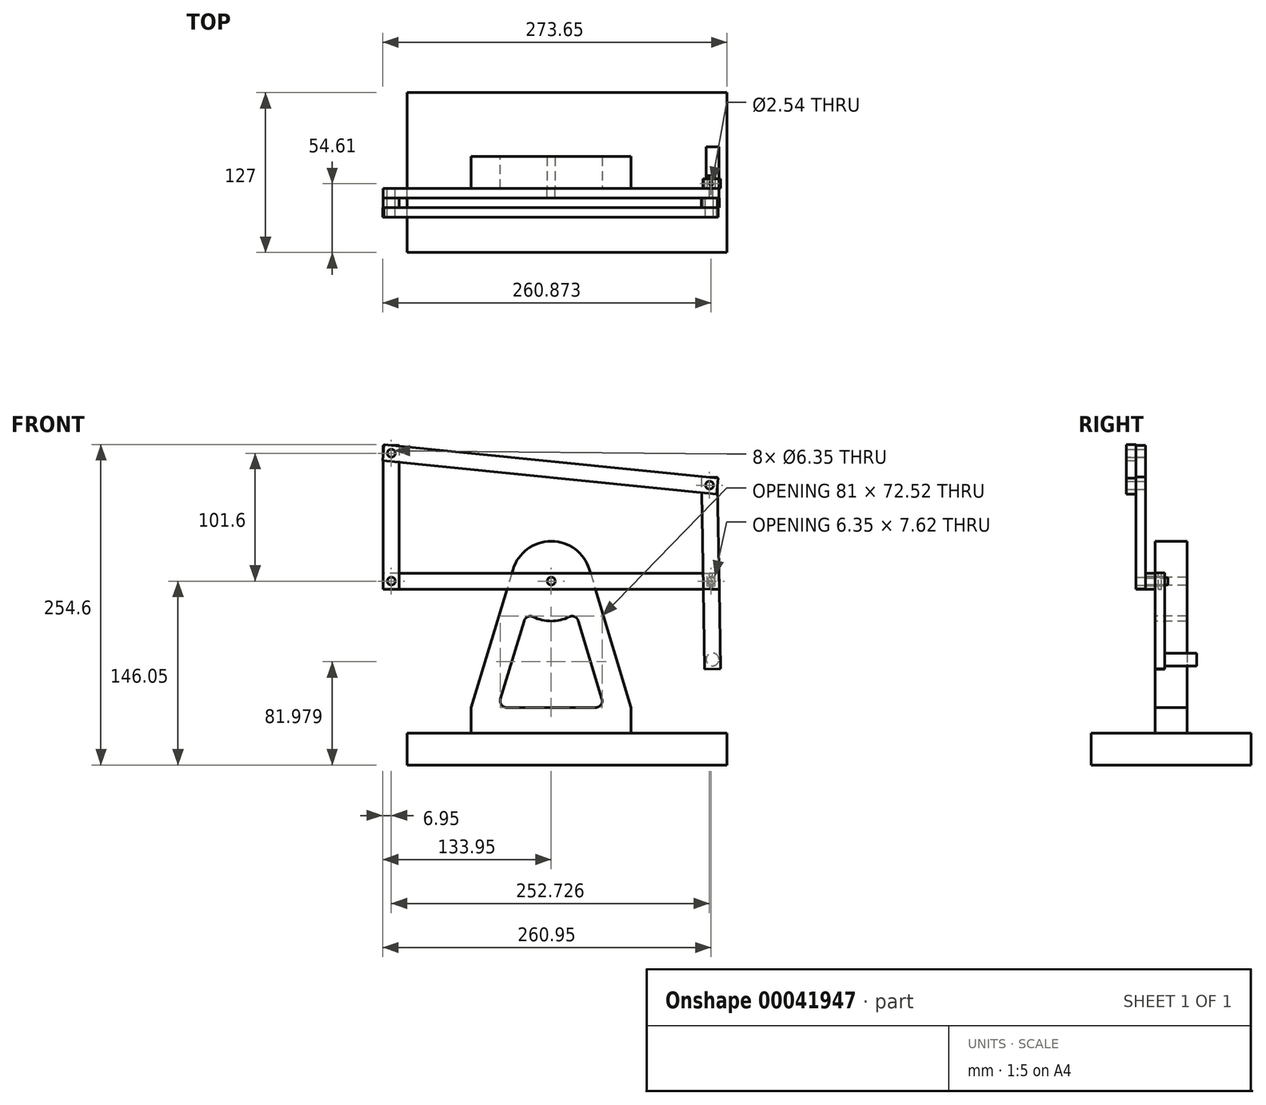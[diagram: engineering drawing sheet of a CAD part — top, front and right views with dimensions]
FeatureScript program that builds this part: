
annotation { "Feature Type Name" : "Feature", "Feature Type Description" : "" }
export const myFeature = defineFeature(function(context is Context, id is Id, definition is map)
    precondition{}
    {
        {
            var Q0;
            Q0=qCreatedBy(makeId("Top.planeOp"),FACE);
            var sketch = newSketch(context, id + "F0", { "sketchPlane" : qUnion([Q0])});
            skLineSegment(sketch, "E0.bottom", {"start": v(0, 0) * mm, "end": v(254, 0) * mm});
            skLineSegment(sketch, "E0.top", {"start": v(0, 127) * mm, "end": v(254, 127) * mm});
            skLineSegment(sketch, "E0.left", {"start": v(0, 0) * mm, "end": v(0, 127) * mm});
            skLineSegment(sketch, "E0.right", {"start": v(254, 0) * mm, "end": v(254, 127) * mm});
            skSolve(sketch);
        }
        {
            var Q0;
            Q0 = qSketchRegion(id + "F0", true);
            extrude(context, id + "F1", {"entities" : qUnion([Q0]), "depth" : 25.4 * mm});
        }
        {
            var Q0;
            Q0=makeQuery(id+"F1.opExtrude","SWEPT_FACE",FACE,{"disambiguationData":[OSD([sQuery(id+"F0.wireOp",EDGE,"E0.bottom")])]});
            var Q1;
            Q1=makeQuery(id+"F1.opExtrude","SWEPT_FACE",FACE,{"disambiguationData":[OSD([sQuery(id+"F0.wireOp",EDGE,"E0.top")])]});
            cPlane(context, id + "F2", {"entities" : qUnion([Q0, Q1]), "cplaneType" : CPlaneType.MID_PLANE, "offset" : 152.4 * mm, "width" : 152.4 * mm, "height" : 152.4 * mm});
        }
        {
            var Q0;
            Q0=qCreatedBy(id+"F2.planeOp",FACE);
            var sketch = newSketch(context, id + "F3", { "sketchPlane" : qUnion([Q0])});
            skLineSegment(sketch, "E1.bottom", {"start": v(50.8, 25.4) * mm, "end": v(177.8, 25.4) * mm});
            skLineSegment(sketch, "E1.top", {"start": v(50.8, 177.8) * mm, "end": v(177.8, 177.8) * mm});
            skLineSegment(sketch, "E1.left", {"start": v(50.8, 25.4) * mm, "end": v(50.8, 177.8) * mm});
            skLineSegment(sketch, "E1.right", {"start": v(177.8, 25.4) * mm, "end": v(177.8, 177.8) * mm});
            skSolve(sketch);
        }
        {
            var Q0;
            Q0 = qSketchRegion(id + "F3", true);
            extrude(context, id + "F4", {"entities" : qUnion([Q0]), "endBound" : BoundingType.SYMMETRIC, "depth" : 25.4 * mm});
        }
        {
            var Q0;
            Q0=makeQuery(id+"F4.opExtrude","CAP_FACE",FACE,{"disambiguationData":[OSD([sQuery(id+"F3.wireOp",EDGE,"E1.bottom"),sQuery(id+"F3.wireOp",EDGE,"E1.top"),sQuery(id+"F3.wireOp",EDGE,"E1.left"),sQuery(id+"F3.wireOp",EDGE,"E1.right")])],"isStart":false});
            var sketch = newSketch(context, id + "F5", { "sketchPlane" : qUnion([Q0])});
            skLineSegment(sketch, "E2", {"start": v(114.3, 25.4) * mm, "end": v(114.3, 177.8) * mm, "construction": true});
            skCircle(sketch, "E3", {"center": v(114.3, 146.05) * mm, "radius": 31.75 * mm});
            skLineSegment(sketch, "E4", {"start": v(83.9, 155.24) * mm, "end": v(50.8, 45.72) * mm});
            skLineSegment(sketch, "E5", {"start": v(144.7, 155.24) * mm, "end": v(177.8, 45.72) * mm});
            skLineSegment(sketch, "E6", {"start": v(50.8, 45.72) * mm, "end": v(177.8, 45.72) * mm});
            skCircle(sketch, "E7", {"center": v(114.3, 146.05) * mm, "radius": 11.43 * mm});
            skLineSegment(sketch, "E8", {"start": v(103.36, 149.36) * mm, "end": v(72.03, 45.72) * mm});
            skLineSegment(sketch, "E9", {"start": v(125.24, 149.36) * mm, "end": v(156.57, 45.72) * mm});
            skSolve(sketch);
        }
        {
            var Q0;
            {var subQ1=sQuery(id+"F5.wireOp",EDGE,"E3");var subQ5=sQuery(id+"F5.wireOp",EDGE,"E8");var subQ6=makeQuery(id+"F5.imprint","INTERSECT",VERTEX,{"derivedFrom":[subQ1,subQ5]});Q0=makeQuery(id+"F5.imprint","IMPRINT",FACE,{"disambiguationData":[TD([[makeQuery(id+"F5.imprint","IMPRINT",EDGE,{"disambiguationData":[TD([[subQ6,-1.0]])],"derivedFrom":subQ1}),-1.0]])]});}
            var Q1;
            {var subQ5=sQuery(id+"F5.wireOp",EDGE,"E4");Q1=makeQuery(id+"F5.imprint","IMPRINT",FACE,{"disambiguationData":[TD([[makeQuery(id+"F5.imprint","IMPRINT",EDGE,{"derivedFrom":subQ5}),-1.0]])]});}
            var Q2;
            {var subQ1=sQuery(id+"F5.wireOp",EDGE,"E5");Q2=makeQuery(id+"F5.imprint","IMPRINT",FACE,{"disambiguationData":[TD([[makeQuery(id+"F5.imprint","IMPRINT",EDGE,{"derivedFrom":subQ1}),1.0]])]});}
            extrude(context, id + "F6", {"entities" : qUnion([Q0, Q1, Q2]), "operationType" : NewBodyOperationType.REMOVE, "endBound" : BoundingType.THROUGH_ALL, "oppositeDirection" : true, "depth" : 25.4 * mm});
        }
        {
            var Q0;
            Q0=makeQuery(id+"F6.boolean.opBoolean","COPY",EDGE,{"derivedFrom":makeQuery(id+"F6.opExtrude","SWEPT_EDGE",EDGE,{"disambiguationData":[OSD([sQuery(id+"F5.wireOp",EDGE,"E6"),sQuery(id+"F5.wireOp",EDGE,"E8")])]})});
            var Q1;
            Q1=makeQuery(id+"F6.boolean.opBoolean","COPY",EDGE,{"derivedFrom":makeQuery(id+"F6.opExtrude","SWEPT_EDGE",EDGE,{"disambiguationData":[OSD([sQuery(id+"F5.wireOp",EDGE,"E6"),sQuery(id+"F5.wireOp",EDGE,"E9")])]})});
            var Q2;
            Q2=makeQuery(id+"F6.boolean.opBoolean","COPY",EDGE,{"derivedFrom":makeQuery(id+"F6.opExtrude","SWEPT_EDGE",EDGE,{"disambiguationData":[OSD([sQuery(id+"F5.wireOp",EDGE,"E3"),sQuery(id+"F5.wireOp",EDGE,"E8")])]})});
            var Q3;
            Q3=makeQuery(id+"F6.boolean.opBoolean","COPY",EDGE,{"derivedFrom":makeQuery(id+"F6.opExtrude","SWEPT_EDGE",EDGE,{"disambiguationData":[OSD([sQuery(id+"F5.wireOp",EDGE,"E3"),sQuery(id+"F5.wireOp",EDGE,"E9")])]})});
            fillet(context, id + "F7", {"entities" : qUnion([Q0, Q1, Q2, Q3]), "radius" : 5.08 * mm, "tangentPropagation" : true, "allowEdgeOverflow" : false});
        }
        {
            var Q0;
            Q0=makeQuery(id+"F4.opExtrude","CAP_FACE",FACE,{"disambiguationData":[OSD([sQuery(id+"F3.wireOp",EDGE,"E1.bottom"),sQuery(id+"F3.wireOp",EDGE,"E1.top"),sQuery(id+"F3.wireOp",EDGE,"E1.left"),sQuery(id+"F3.wireOp",EDGE,"E1.right")])],"isStart":false});
            var sketch = newSketch(context, id + "F8", { "sketchPlane" : qUnion([Q0])});
            skLineSegment(sketch, "E10", {"start": v(-12.7, 146.05) * mm, "end": v(241.3, 146.05) * mm, "construction": true});
            skPoint(sketch, "E11", {"position": v(114.3, 146.05) * mm});
            skLineSegment(sketch, "E12", {"start": v(-12.7, 146.05) * mm, "end": v(-12.7, 247.65) * mm, "construction": true});
            skLineSegment(sketch, "E13", {"start": v(-12.7, 247.65) * mm, "end": v(240.03, 222.24) * mm, "construction": true});
            skLineSegment(sketch, "E14", {"start": v(240.03, 222.24) * mm, "end": v(241.3, 146.05) * mm, "construction": true});
            skSolve(sketch);
        }
        {
            var Q0;
            {var subQ6=sQuery(id+"F3.wireOp",EDGE,"E1.bottom");Q0=makeQuery(id+"F8.imprint","IMPRINT",FACE,{"disambiguationData":[TD([[makeQuery(id+"F8.imprint","IMPRINT",EDGE,{"derivedFrom":makeQuery(id+"F4.opExtrude","CAP_EDGE",EDGE,{"disambiguationData":[OSD([subQ6])],"isStart":false})}),1.0]])]});}
            var sketch = newSketch(context, id + "F9", { "sketchPlane" : qUnion([Q0])});
            skLineSegment(sketch, "E15.rect.bottom", {"start": v(247.65, 139.7) * mm, "end": v(-19.05, 139.7) * mm});
            skLineSegment(sketch, "E15.rect.top", {"start": v(247.65, 152.4) * mm, "end": v(-19.05, 152.4) * mm});
            skLineSegment(sketch, "E15.rect.left", {"start": v(247.65, 139.7) * mm, "end": v(247.65, 152.4) * mm});
            skLineSegment(sketch, "E15.rect.right", {"start": v(-19.05, 139.7) * mm, "end": v(-19.05, 152.4) * mm});
            skPoint(sketch, "E15.rect.middle", {"position": v(114.3, 146.05) * mm});
            skSolve(sketch);
        }
        {
            var Q0;
            Q0 = qSketchRegion(id + "F9", true);
            extrude(context, id + "F10", {"entities" : qUnion([Q0]), "depth" : 7.62 * mm});
        }
        {
            var Q0;
            Q0=makeQuery(id+"F10.opExtrude","CAP_FACE",FACE,{"disambiguationData":[OSD([sQuery(id+"F9.wireOp",EDGE,"E15.rect.bottom"),sQuery(id+"F9.wireOp",EDGE,"E15.rect.top"),sQuery(id+"F9.wireOp",EDGE,"E15.rect.left"),sQuery(id+"F9.wireOp",EDGE,"E15.rect.right")])],"isStart":false});
            var sketch = newSketch(context, id + "F11", { "sketchPlane" : qUnion([Q0])});
            skLineSegment(sketch, "E16.rect.bottom", {"start": v(-6.35, 254) * mm, "end": v(-19.05, 254) * mm});
            skLineSegment(sketch, "E16.rect.top", {"start": v(-6.35, 139.7) * mm, "end": v(-19.05, 139.7) * mm});
            skLineSegment(sketch, "E16.rect.left", {"start": v(-6.35, 254) * mm, "end": v(-6.35, 139.7) * mm});
            skLineSegment(sketch, "E16.rect.right", {"start": v(-19.05, 254) * mm, "end": v(-19.05, 139.7) * mm});
            skPoint(sketch, "E16.rect.middle", {"position": v(-12.7, 196.85) * mm});
            skLineSegment(sketch, "E17", {"start": v(-12.7, 254) * mm, "end": v(-12.7, 139.7) * mm, "construction": true});
            skSolve(sketch);
        }
        {
            var Q0;
            Q0 = qSketchRegion(id + "F11", true);
            extrude(context, id + "F12", {"entities" : qUnion([Q0]), "depth" : 7.62 * mm});
        }
        {
            var Q0;
            Q0=makeQuery(id+"F12.opExtrude","CAP_FACE",FACE,{"disambiguationData":[OSD([sQuery(id+"F11.wireOp",EDGE,"E16.rect.bottom"),sQuery(id+"F11.wireOp",EDGE,"E16.rect.top"),sQuery(id+"F11.wireOp",EDGE,"E16.rect.left"),sQuery(id+"F11.wireOp",EDGE,"E16.rect.right")])],"isStart":false});
            var sketch = newSketch(context, id + "F13", { "sketchPlane" : qUnion([Q0])});
            skLineSegment(sketch, "E18.rect.bottom", {"start": v(245.7, 215.29) * mm, "end": v(-19.65, 241.97) * mm});
            skLineSegment(sketch, "E18.rect.top", {"start": v(246.98, 227.92) * mm, "end": v(-18.38, 254.6) * mm});
            skLineSegment(sketch, "E18.rect.left", {"start": v(245.7, 215.29) * mm, "end": v(246.98, 227.92) * mm});
            skLineSegment(sketch, "E18.rect.right", {"start": v(-19.65, 241.97) * mm, "end": v(-18.38, 254.6) * mm});
            skPoint(sketch, "E18.rect.middle", {"position": v(113.66, 234.94) * mm});
            skLineSegment(sketch, "E19", {"start": v(246.34, 221.6) * mm, "end": v(-19.02, 248.29) * mm, "construction": true});
            skSolve(sketch);
        }
        {
            var Q0;
            Q0 = qSketchRegion(id + "F13", true);
            extrude(context, id + "F14", {"entities" : qUnion([Q0]), "depth" : 7.62 * mm});
        }
        {
            var Q0;
            Q0=makeQuery(id+"F10.opExtrude","CAP_FACE",FACE,{"disambiguationData":[OSD([sQuery(id+"F9.wireOp",EDGE,"E15.rect.bottom"),sQuery(id+"F9.wireOp",EDGE,"E15.rect.top"),sQuery(id+"F9.wireOp",EDGE,"E15.rect.left"),sQuery(id+"F9.wireOp",EDGE,"E15.rect.right")])],"isStart":false});
            var sketch = newSketch(context, id + "F15", { "sketchPlane" : qUnion([Q0])});
            skLineSegment(sketch, "E20.rect.bottom", {"start": v(246.27, 228.7) * mm, "end": v(233.57, 228.48) * mm});
            skLineSegment(sketch, "E20.rect.top", {"start": v(247.76, 139.8) * mm, "end": v(235.06, 139.6) * mm});
            skLineSegment(sketch, "E20.rect.left", {"start": v(246.27, 228.7) * mm, "end": v(247.76, 139.8) * mm});
            skLineSegment(sketch, "E20.rect.right", {"start": v(233.57, 228.48) * mm, "end": v(235.06, 139.6) * mm});
            skPoint(sketch, "E20.rect.middle", {"position": v(240.66, 184.14) * mm});
            skLineSegment(sketch, "E21", {"start": v(239.92, 228.59) * mm, "end": v(241.4, 139.7) * mm, "construction": true});
            skSolve(sketch);
        }
        {
            var Q0;
            Q0 = qSketchRegion(id + "F15", true);
            extrude(context, id + "F16", {"entities" : qUnion([Q0]), "depth" : 7.62 * mm});
        }
        {
            var Q0;
            Q0=sQuery(id+"F8.wireOp",VERTEX,"E13.start");
            var Q1;
            Q1=sQuery(id+"F8.wireOp",VERTEX,"E10.start");
            var Q2;
            Q2=sQuery(id+"F8.wireOp",VERTEX,"E11");
            var Q3;
            Q3=sQuery(id+"F8.wireOp",VERTEX,"E10.end");
            var Q4;
            Q4=sQuery(id+"F8.wireOp",VERTEX,"E14.start");
            var Q5;
            Q5=makeQuery(id+"F12.opExtrude","SWEPT_BODY",BODY,{"disambiguationData":[OSD([sQuery(id+"F11.wireOp",EDGE,"E16.rect.bottom"),sQuery(id+"F11.wireOp",EDGE,"E16.rect.top"),sQuery(id+"F11.wireOp",EDGE,"E16.rect.left"),sQuery(id+"F11.wireOp",EDGE,"E16.rect.right")])]});
            var Q6;
            Q6=makeQuery(id+"F14.opExtrude","SWEPT_BODY",BODY,{"disambiguationData":[OSD([sQuery(id+"F13.wireOp",EDGE,"E18.rect.bottom"),sQuery(id+"F13.wireOp",EDGE,"E18.rect.top"),sQuery(id+"F13.wireOp",EDGE,"E18.rect.left"),sQuery(id+"F13.wireOp",EDGE,"E18.rect.right")])]});
            var Q7;
            Q7=makeQuery(id+"F10.opExtrude","SWEPT_BODY",BODY,{"disambiguationData":[OSD([sQuery(id+"F9.wireOp",EDGE,"E15.rect.bottom"),sQuery(id+"F9.wireOp",EDGE,"E15.rect.top"),sQuery(id+"F9.wireOp",EDGE,"E15.rect.left"),sQuery(id+"F9.wireOp",EDGE,"E15.rect.right")])]});
            var Q8;
            Q8=makeQuery(id+"F4.opExtrude","SWEPT_BODY",BODY,{"disambiguationData":[OSD([sQuery(id+"F3.wireOp",EDGE,"E1.bottom"),sQuery(id+"F3.wireOp",EDGE,"E1.top"),sQuery(id+"F3.wireOp",EDGE,"E1.left"),sQuery(id+"F3.wireOp",EDGE,"E1.right")])]});
            var Q9;
            Q9=makeQuery(id+"F16.opExtrude","SWEPT_BODY",BODY,{"disambiguationData":[OSD([sQuery(id+"F15.wireOp",EDGE,"E20.rect.bottom"),sQuery(id+"F15.wireOp",EDGE,"E20.rect.top"),sQuery(id+"F15.wireOp",EDGE,"E20.rect.left"),sQuery(id+"F15.wireOp",EDGE,"E20.rect.right")])]});
            hole(context, id + "F17", {"style" : HoleStyle.SIMPLE, "holeDiameter" : 6.35 * mm, "endStyle" : HoleEndStyle.THROUGH, "oppositeDirection" : true, "locations" : qUnion([Q0, Q1, Q2, Q3, Q4]), "scope" : qUnion([Q5, Q6, Q7, Q8, Q9])});
        }
        {
            var Q0;
            Q0=sQuery(id+"F8.wireOp",VERTEX,"E11");
            var Q1;
            Q1=makeQuery(id+"F4.opExtrude","SWEPT_BODY",BODY,{"disambiguationData":[OSD([sQuery(id+"F3.wireOp",EDGE,"E1.bottom"),sQuery(id+"F3.wireOp",EDGE,"E1.top"),sQuery(id+"F3.wireOp",EDGE,"E1.left"),sQuery(id+"F3.wireOp",EDGE,"E1.right")])]});
            hole(context, id + "F18", {"style" : HoleStyle.SIMPLE, "holeDiameter" : 6.35 * mm, "endStyle" : HoleEndStyle.THROUGH, "locations" : qUnion([Q0]), "scope" : qUnion([Q1])});
        }
        {
            var Q0;
            Q0=makeQuery(id+"F16.opExtrude","CAP_FACE",FACE,{"disambiguationData":[OSD([sQuery(id+"F15.wireOp",EDGE,"E20.rect.bottom"),sQuery(id+"F15.wireOp",EDGE,"E20.rect.top"),sQuery(id+"F15.wireOp",EDGE,"E20.rect.left"),sQuery(id+"F15.wireOp",EDGE,"E20.rect.right")])],"isStart":false});
            var sketch = newSketch(context, id + "F19", { "sketchPlane" : qUnion([Q0])});
            skCircle(sketch, "E22.0", {"center": v(241.3, 146.05) * mm, "radius": 3.18 * mm});
            skSolve(sketch);
        }
        {
            var Q0;
            Q0=makeQuery(id+"F10.opExtrude","CAP_FACE",FACE,{"disambiguationData":[OSD([sQuery(id+"F9.wireOp",EDGE,"E15.rect.bottom"),sQuery(id+"F9.wireOp",EDGE,"E15.rect.top"),sQuery(id+"F9.wireOp",EDGE,"E15.rect.left"),sQuery(id+"F9.wireOp",EDGE,"E15.rect.right")])],"isStart":true});
            var sketch = newSketch(context, id + "F20", { "sketchPlane" : qUnion([Q0])});
            skLineSegment(sketch, "E23.rect.bottom", {"start": v(-236.12, 76.1) * mm, "end": v(-248.82, 76.32) * mm});
            skLineSegment(sketch, "E23.rect.top", {"start": v(-234.84, 152.3) * mm, "end": v(-247.54, 152.5) * mm});
            skLineSegment(sketch, "E23.rect.left", {"start": v(-236.12, 76.1) * mm, "end": v(-234.84, 152.3) * mm});
            skLineSegment(sketch, "E23.rect.right", {"start": v(-248.82, 76.32) * mm, "end": v(-247.54, 152.5) * mm});
            skPoint(sketch, "E23.rect.middle", {"position": v(-241.83, 114.3) * mm});
            skLineSegment(sketch, "E24", {"start": v(-242.47, 76.2) * mm, "end": v(-241.2, 152.4) * mm, "construction": true});
            skSolve(sketch);
        }
        {
            var Q0;
            Q0 = qSketchRegion(id + "F20", true);
            extrude(context, id + "F21", {"entities" : qUnion([Q0]), "depth" : 7.62 * mm});
        }
        {
            var Q0;
            Q0=makeQuery(id+"F21.boolean.opBoolean","MERGE",FACE,{"derivedFrom":[makeQuery(id+"Fn6mMpEegykz9fj_6.opExtrude","CAP_FACE",FACE,{"disambiguationData":[OSD([sQuery(id+"F19.wireOp",EDGE,"E22.0")])],"isStart":false}),makeQuery(id+"F21.opExtrude","CAP_FACE",FACE,{"disambiguationData":[OSD([sQuery(id+"F20.wireOp",EDGE,"E23.rect.bottom"),sQuery(id+"F20.wireOp",EDGE,"E23.rect.top"),sQuery(id+"F20.wireOp",EDGE,"E23.rect.left"),sQuery(id+"F20.wireOp",EDGE,"E23.rect.right")])],"isStart":false})]});
            var sketch = newSketch(context, id + "F22", { "sketchPlane" : qUnion([Q0])});
            skCircle(sketch, "E25", {"center": v(-242.47, 83.83) * mm, "radius": 5.08 * mm});
            skPoint(sketch, "E25.centerSnap0", {"position": v(-242.47, 76.2) * mm});
            skSolve(sketch);
        }
        {
            var Q0;
            Q0 = qSketchRegion(id + "F22", true);
            extrude(context, id + "F23", {"entities" : qUnion([Q0]), "operationType" : NewBodyOperationType.ADD, "depth" : 25.4 * mm});
        }
        {
            var Q0;
            Q0=makeQuery(id+"F14.opExtrude","CAP_FACE",FACE,{"disambiguationData":[OSD([sQuery(id+"F13.wireOp",EDGE,"E18.rect.bottom"),sQuery(id+"F13.wireOp",EDGE,"E18.rect.top"),sQuery(id+"F13.wireOp",EDGE,"E18.rect.left"),sQuery(id+"F13.wireOp",EDGE,"E18.rect.right")])],"isStart":false});
            var sketch = newSketch(context, id + "F24", { "sketchPlane" : qUnion([Q0])});
            skCircle(sketch, "E26.0", {"center": v(-12.7, 247.65) * mm, "radius": 3.18 * mm});
            skSolve(sketch);
        }
        {
            var Q0;
            Q0 = qSketchRegion(id + "F24", true);
            extrude(context, id + "F25", {"entities" : qUnion([Q0]), "oppositeDirection" : true, "depth" : 15.24 * mm});
        }
        {
            var Q0;
            Q0=sQuery(id+"F19.wireOp",VERTEX,"E22.0.center");
            var Q1;
            Q1=makeQuery(id+"F21.opExtrude","SWEPT_BODY",BODY,{"disambiguationData":[OSD([sQuery(id+"F20.wireOp",EDGE,"E23.rect.bottom"),sQuery(id+"F20.wireOp",EDGE,"E23.rect.top"),sQuery(id+"F20.wireOp",EDGE,"E23.rect.left"),sQuery(id+"F20.wireOp",EDGE,"E23.rect.right")])]});
            hole(context, id + "F26", {"style" : HoleStyle.SIMPLE, "holeDiameter" : 6.35 * mm, "endStyle" : HoleEndStyle.THROUGH, "locations" : qUnion([Q0]), "scope" : qUnion([Q1])});
        }
        {
            var Q0;
            Q0=makeQuery(id+"F16.opExtrude","CAP_FACE",FACE,{"disambiguationData":[OSD([sQuery(id+"F15.wireOp",EDGE,"E20.rect.bottom"),sQuery(id+"F15.wireOp",EDGE,"E20.rect.top"),sQuery(id+"F15.wireOp",EDGE,"E20.rect.left"),sQuery(id+"F15.wireOp",EDGE,"E20.rect.right")])],"isStart":false});
            var sketch = newSketch(context, id + "F27", { "sketchPlane" : qUnion([Q0])});
            skLineSegment(sketch, "E27.rect.bottom", {"start": v(242.57, 142.24) * mm, "end": v(240.03, 142.24) * mm});
            skLineSegment(sketch, "E27.rect.top", {"start": v(242.57, 149.86) * mm, "end": v(240.03, 149.86) * mm});
            skLineSegment(sketch, "E27.rect.left", {"start": v(242.57, 142.24) * mm, "end": v(242.57, 149.86) * mm});
            skLineSegment(sketch, "E27.rect.right", {"start": v(240.03, 142.24) * mm, "end": v(240.03, 149.86) * mm});
            skPoint(sketch, "E27.rect.middle", {"position": v(241.3, 146.05) * mm});
            skSolve(sketch);
        }
        {
            var Q0;
            Q0 = qSketchRegion(id + "F27", true);
            extrude(context, id + "F28", {"entities" : qUnion([Q0]), "operationType" : NewBodyOperationType.REMOVE, "endBound" : BoundingType.THROUGH_ALL, "oppositeDirection" : true, "depth" : 25.4 * mm});
        }
        {
            var Q0;
            Q0=makeQuery(id+"F16.opExtrude","CAP_FACE",FACE,{"disambiguationData":[OSD([sQuery(id+"F15.wireOp",EDGE,"E20.rect.bottom"),sQuery(id+"F15.wireOp",EDGE,"E20.rect.top"),sQuery(id+"F15.wireOp",EDGE,"E20.rect.left"),sQuery(id+"F15.wireOp",EDGE,"E20.rect.right")])],"isStart":false});
            var sketch = newSketch(context, id + "F29", { "sketchPlane" : qUnion([Q0])});
            skLineSegment(sketch, "E28.0", {"start": v(242.57, 149.86) * mm, "end": v(240.03, 149.86) * mm});
            skPoint(sketch, "E29.0", {"position": v(242.57, 148.96) * mm});
            skArc(sketch, "E30.0", {"start": v(242.57, 148.96) * mm, "mid": v(244.48, 146.05) * mm, "end": v(242.57, 143.14) * mm});
            skLineSegment(sketch, "E31.0", {"start": v(240.03, 148.96) * mm, "end": v(240.03, 149.86) * mm});
            skLineSegment(sketch, "E32.0", {"start": v(242.57, 148.96) * mm, "end": v(242.57, 149.86) * mm});
            skLineSegment(sketch, "E33.0", {"start": v(242.57, 142.24) * mm, "end": v(242.57, 143.14) * mm});
            skLineSegment(sketch, "E34.0", {"start": v(242.57, 142.24) * mm, "end": v(240.03, 142.24) * mm});
            skLineSegment(sketch, "E35.0", {"start": v(240.03, 142.24) * mm, "end": v(240.03, 143.14) * mm});
            skArc(sketch, "E36.0", {"start": v(240.03, 143.14) * mm, "mid": v(238.12, 146.05) * mm, "end": v(240.03, 148.96) * mm});
            skCircle(sketch, "E37", {"center": v(241.3, 146.05) * mm, "radius": 3.18 * mm});
            skSolve(sketch);
        }
        {
            var Q0;
            {var subQ0=sQuery(id+"F29.wireOp",EDGE,"E37");var subQ1=makeQuery(id+"F29.imprint","INTERSECT",VERTEX,{"derivedFrom":[sQuery(id+"F29.wireOp",EDGE,"E31.0"),subQ0]});var subQ4=makeQuery(id+"F29.imprint","INTERSECT",VERTEX,{"derivedFrom":[sQuery(id+"F29.wireOp",EDGE,"E32.0"),subQ0]});Q0=makeQuery(id+"F29.imprint","IMPRINT",FACE,{"disambiguationData":[TD([[makeQuery(id+"F29.imprint","IMPRINT",EDGE,{"disambiguationData":[TD([[subQ4,-1.0],[subQ1,1.0]])],"derivedFrom":subQ0}),1.0]])]});}
            extrude(context, id + "F30", {"entities" : qUnion([Q0]), "oppositeDirection" : true, "depth" : 25.4 * mm});
        }
        {
            var Q0;
            Q0 = qSketchRegion(id + "F29", true);
            extrude(context, id + "F31", {"entities" : qUnion([Q0]), "operationType" : NewBodyOperationType.ADD, "oppositeDirection" : true, "depth" : 7.62 * mm});
        }
        {
            var Q0;
            Q0=makeQuery(id+"F30.opExtrude","CAP_FACE",FACE,{"disambiguationData":[OSD([sQuery(id+"F29.wireOp",EDGE,"E37")])],"isStart":false});
            var sketch = newSketch(context, id + "F32", { "sketchPlane" : qUnion([Q0])});
            skLineSegment(sketch, "E38.bottom", {"start": v(-242.57, 149.86) * mm, "end": v(-240.03, 149.86) * mm});
            skLineSegment(sketch, "E38.top", {"start": v(-242.57, 148.6) * mm, "end": v(-240.03, 148.6) * mm});
            skLineSegment(sketch, "E38.left", {"start": v(-242.57, 149.86) * mm, "end": v(-242.57, 148.6) * mm});
            skLineSegment(sketch, "E38.right", {"start": v(-240.03, 149.86) * mm, "end": v(-240.03, 148.6) * mm});
            skLineSegment(sketch, "E39.bottom", {"start": v(-240.03, 143.51) * mm, "end": v(-242.57, 143.51) * mm});
            skLineSegment(sketch, "E39.top", {"start": v(-240.03, 142.24) * mm, "end": v(-242.57, 142.24) * mm});
            skLineSegment(sketch, "E39.left", {"start": v(-240.03, 143.51) * mm, "end": v(-240.03, 142.24) * mm});
            skLineSegment(sketch, "E39.right", {"start": v(-242.57, 143.51) * mm, "end": v(-242.57, 142.24) * mm});
            skSolve(sketch);
        }
        {
            var Q0;
            Q0 = qSketchRegion(id + "F32", true);
            var Q1;
            {var subQ0=sQuery(id+"F29.wireOp",EDGE,"E28.0");var subQ1=sQuery(id+"F29.wireOp",EDGE,"E31.0");var subQ2=sQuery(id+"F29.wireOp",EDGE,"E32.0");var subQ3=sQuery(id+"F29.wireOp",EDGE,"E37");Q1=makeQuery(id+"F31.boolean.opBoolean","SPLIT",FACE,{"disambiguationData":[TD([makeQuery(id+"F31.opExtrude","SWEPT_FACE",FACE,{"disambiguationData":[OSD([subQ0])]})])],"derivedFrom":makeQuery(id+"F31.opExtrude","CAP_FACE",FACE,{"disambiguationData":[OSD([subQ0,subQ1,subQ2,sQuery(id+"F29.wireOp",EDGE,"E33.0"),sQuery(id+"F29.wireOp",EDGE,"E34.0"),sQuery(id+"F29.wireOp",EDGE,"E35.0"),subQ3])],"isStart":false})});}
            extrude(context, id + "F33", {"entities" : qUnion([Q0]), "operationType" : NewBodyOperationType.REMOVE, "endBound" : BoundingType.UP_TO_SURFACE, "oppositeDirection" : true, "endBoundEntityFace" : qUnion([Q1]), "depth" : 25.4 * mm});
        }
        {
            var Q0;
            Q0=makeQuery(id+"F21.opExtrude","SWEPT_FACE",FACE,{"disambiguationData":[OSD([sQuery(id+"F20.wireOp",EDGE,"E23.rect.top")])]});
            var sketch = newSketch(context, id + "F34", { "sketchPlane" : qUnion([Q0])});
            skLineSegment(sketch, "E40.bottom", {"start": v(250.06, 50.8) * mm, "end": v(237.36, 50.8) * mm});
            skLineSegment(sketch, "E40.top", {"start": v(250.06, 58.42) * mm, "end": v(237.36, 58.42) * mm});
            skLineSegment(sketch, "E40.left", {"start": v(250.06, 50.8) * mm, "end": v(250.06, 58.42) * mm});
            skLineSegment(sketch, "E40.right", {"start": v(237.36, 50.8) * mm, "end": v(237.36, 58.42) * mm});
            skLineSegment(sketch, "E41", {"start": v(237.36, 54.6) * mm, "end": v(250.06, 54.6) * mm});
            skPoint(sketch, "E42", {"position": v(243.7, 54.6) * mm});
            skSolve(sketch);
        }
        {
            var Q0;
            Q0=sQuery(id+"F34.wireOp",VERTEX,"E42");
            var Q1;
            Q1=makeQuery(id+"F21.opExtrude","SWEPT_BODY",BODY,{"disambiguationData":[OSD([sQuery(id+"F20.wireOp",EDGE,"E23.rect.bottom"),sQuery(id+"F20.wireOp",EDGE,"E23.rect.top"),sQuery(id+"F20.wireOp",EDGE,"E23.rect.left"),sQuery(id+"F20.wireOp",EDGE,"E23.rect.right")])]});
            hole(context, id + "F35", {"style" : HoleStyle.SIMPLE, "holeDiameter" : 2.54 * mm, "endStyle" : HoleEndStyle.BLIND, "holeDepth" : 7.62 * mm, "locations" : qUnion([Q0]), "scope" : qUnion([Q1])});
        }
        {
            var Q0;
            Q0=makeQuery(id+"F21.opExtrude","SWEPT_FACE",FACE,{"disambiguationData":[OSD([sQuery(id+"F20.wireOp",EDGE,"E23.rect.top")])]});
            var sketch = newSketch(context, id + "F36", { "sketchPlane" : qUnion([Q0])});
            skCircle(sketch, "E43.0", {"center": v(243.7, 54.6) * mm, "radius": 1.27 * mm});
            skSolve(sketch);
        }
        {
            var Q0;
            Q0 = qSketchRegion(id + "F36", true);
            extrude(context, id + "F37", {"entities" : qUnion([Q0]), "oppositeDirection" : true, "depth" : 12.7 * mm});
        }
    });
